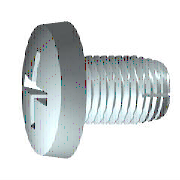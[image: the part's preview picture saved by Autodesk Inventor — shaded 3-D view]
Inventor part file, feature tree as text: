
AUTODESK INVENTOR PART (.ipt)
format: ipt  version: 2024.1 (Build 281209000, 209)  size: 283,648 bytes
history: native  units: mm (DEFAULTED — no unit token found)
features: other x2, extrude x1, plane x1
ambient origin geometry x8: Origin, YZ Plane, XZ Plane, XY Plane, X Axis, Y Axis, Z Axis, Center Point
bodies: Solid1 (feature_tree), Body (feature_tree)
feature tree (4):
  other  "IDS_WORKPLANE{1}"
  extrude  "Slot"  Depth=3.0mm
  other  "Cut"
  plane  "Work Plane3"
